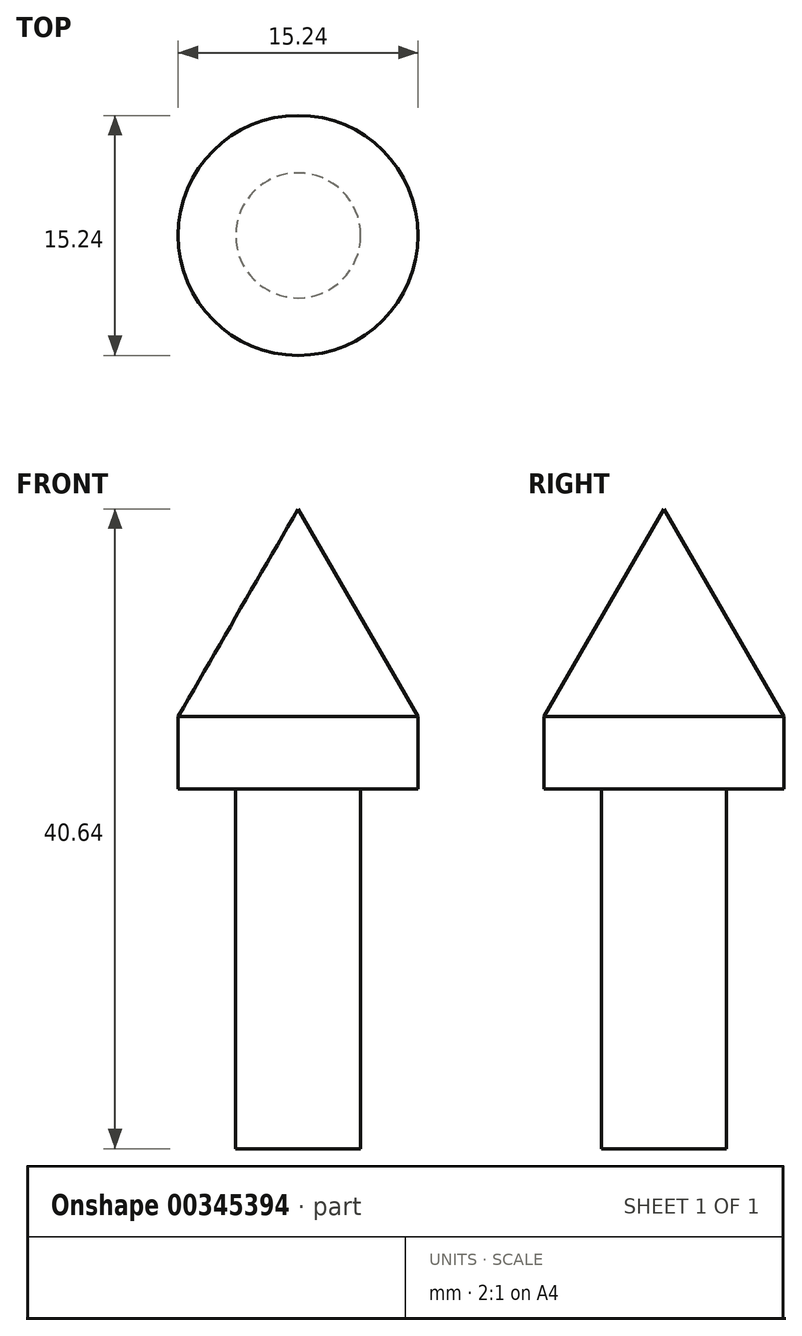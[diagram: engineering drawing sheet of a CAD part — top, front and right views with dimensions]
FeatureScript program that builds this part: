
annotation { "Feature Type Name" : "Feature", "Feature Type Description" : "" }
export const myFeature = defineFeature(function(context is Context, id is Id, definition is map)
    precondition{}
    {
        {
            var Q0;
            Q0=qCreatedBy(makeId("Top.planeOp"),FACE);
            var sketch = newSketch(context, id + "F0", { "sketchPlane" : qUnion([Q0])});
            skCircle(sketch, "E0", {"center": v(0, 0) * mm, "radius": 3.97 * mm});
            skSolve(sketch);
        }
        {
            var Q0;
            Q0=makeQuery(id+"F0.imprint","IMPRINT",FACE,{"disambiguationData":[TD([[makeQuery(id+"F0.imprint","IMPRINT",EDGE,{"derivedFrom":sQuery(id+"F0.wireOp",EDGE,"E0")}),1.0]])]});
            extrude(context, id + "F1", {"entities" : qUnion([Q0]), "depth" : 22.86 * mm});
        }
        {
            var Q0;
            Q0=makeQuery(id+"F1.opExtrude","CAP_FACE",FACE,{"disambiguationData":[OSD([sQuery(id+"F0.wireOp",EDGE,"E0")])],"isStart":false});
            var sketch = newSketch(context, id + "F2", { "sketchPlane" : qUnion([Q0])});
            skCircle(sketch, "E1", {"center": v(0, 0) * mm, "radius": 7.62 * mm});
            skSolve(sketch);
        }
        {
            var Q0;
            Q0=makeQuery(id+"F2.imprint","IMPRINT",FACE,{"disambiguationData":[TD([[makeQuery(id+"F2.imprint","IMPRINT",EDGE,{"derivedFrom":makeQuery(id+"F1.opExtrude","CAP_EDGE",EDGE,{"disambiguationData":[OSD([sQuery(id+"F0.wireOp",EDGE,"E0")])],"isStart":false})}),1.0]])]});
            var Q1;
            Q1=makeQuery(id+"F2.imprint","IMPRINT",FACE,{"disambiguationData":[TD([[makeQuery(id+"F2.imprint","IMPRINT",EDGE,{"derivedFrom":sQuery(id+"F2.wireOp",EDGE,"E1")}),1.0]])]});
            extrude(context, id + "F3", {"entities" : qUnion([Q0, Q1]), "operationType" : NewBodyOperationType.ADD, "depth" : 17.78 * mm});
        }
        {
            var Q0;
            Q0=makeQuery(id+"F3.opExtrude","CAP_EDGE",EDGE,{"disambiguationData":[OSD([sQuery(id+"F2.wireOp",EDGE,"E1")])],"isStart":false});
            chamfer(context, id + "F4", {"entities" : qUnion([Q0]), "chamferType" : ChamferType.OFFSET_ANGLE, "width" : 7.62 * mm, "oppositeDirection" : false, "angle" : 60 * degree, "tangentPropagation" : true});
        }
    });
